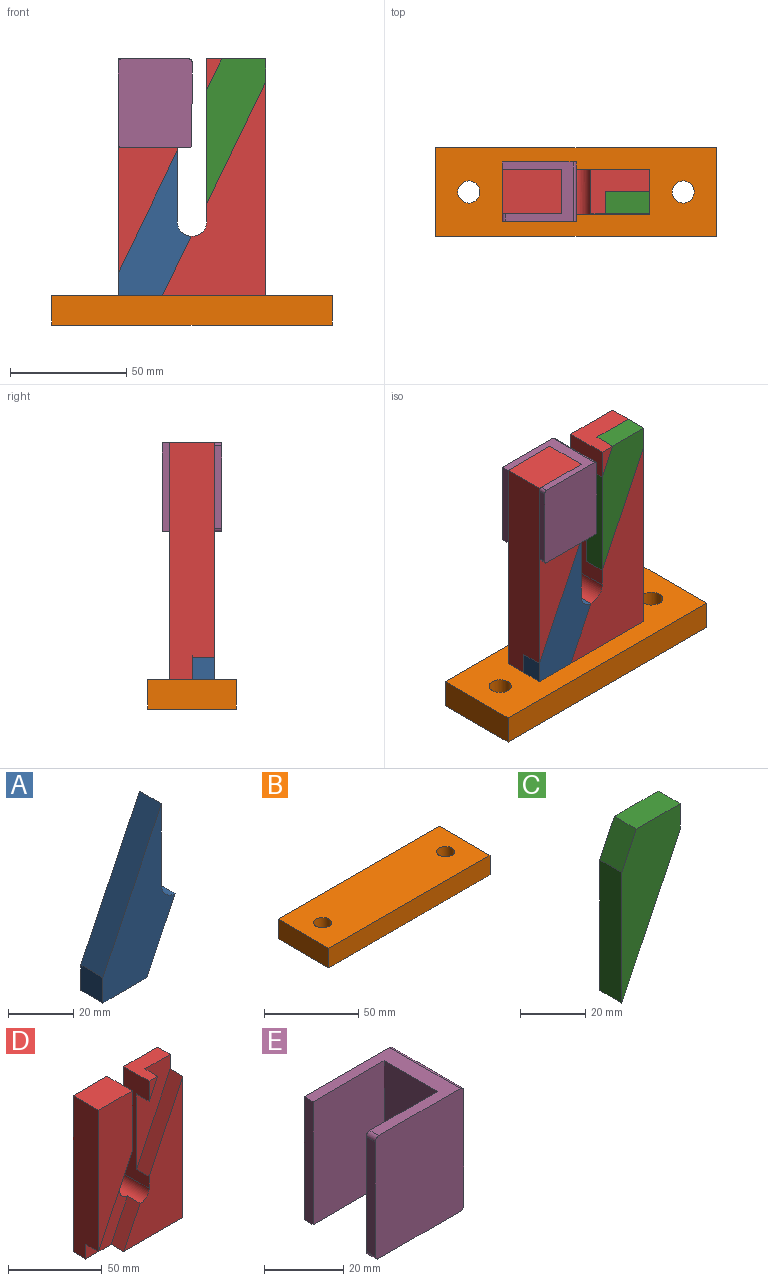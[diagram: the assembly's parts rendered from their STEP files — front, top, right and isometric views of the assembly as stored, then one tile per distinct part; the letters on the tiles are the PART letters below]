
ASSEMBLY  parts=5 mates=4
PART A: 8 faces, bbox 31.3x9.5x62.1 mm
  f0: plane 52.61x25.4mm, normal (-0.9,0,0.43), area 556.5mm2, adj f1,f5,f6,f7
  f1: plane 9.53x9.53mm, normal (-1,0,0), area 90.7mm2, adj f0,f2,f6,f7
  f2: plane 19.05x9.53mm, normal (0,0,-1), area 181.5mm2, adj f1,f3,f6,f7
  f3: plane 25.41x12.27mm, normal (0.9,0,-0.43), area 268.8mm2, adj f2,f4,f6,f7
  f4: cylinder r=6.35mm len=9.53mm, axis (0,1,0), area 90.9mm2, adj f3,f5,f6,f7
  f5: plane 30.39x9.53mm, normal (1,0,0), area 289.5mm2, adj f0,f4,f6,f7
  f6: plane 62.14x31.32mm, normal (0,-1,0), area 913.2mm2, adj f0,f1,f2,f3,f4,f5
  f7: plane 62.14x31.32mm, normal (0,1,0), area 913.2mm2, adj f0,f1,f2,f3,f4,f5
PART B: 8 faces, bbox 120.7x38.1x12.7 mm
  f0: plane 120.65x12.7mm, normal (0,-1,0), area 1532.3mm2, adj f1,f3,f4,f5
  f1: plane 38.1x12.7mm, normal (1,0,0), area 483.9mm2, adj f0,f2,f4,f5
  f2: plane 120.65x12.7mm, normal (0,1,0), area 1532.3mm2, adj f1,f3,f4,f5
  f3: plane 38.1x12.7mm, normal (-1,0,0), area 483.9mm2, adj f0,f2,f4,f5
  f4: plane 120.65x38.1mm, normal (0,0,1), area 4454.3mm2, adj f0,f1,f2,f3,f6,f7
  f5: plane 120.65x38.1mm, normal (0,0,-1), area 4454.3mm2, adj f0,f1,f2,f3,f6,f7
  f6: cylinder r=4.76mm len=12.7mm, axis (0,0,1), area 380mm2, adj f4,f5
  f7: cylinder r=4.76mm len=12.7mm, axis (0,0,1), area 380mm2, adj f4,f5
PART C: 7 faces, bbox 25.4x9.5x62.1 mm
  f0: plane 13.15x9.53mm, normal (-0.9,0,0.43), area 139.1mm2, adj f1,f4,f5,f6
  f1: plane 48.99x9.53mm, normal (-1,0,0), area 466.6mm2, adj f0,f2,f5,f6
  f2: plane 52.61x25.4mm, normal (0.9,0,-0.43), area 556.5mm2, adj f1,f3,f5,f6
  f3: plane 9.53x9.53mm, normal (1,0,0), area 90.7mm2, adj f2,f4,f5,f6
  f4: plane 19.05x9.53mm, normal (0,0,1), area 181.5mm2, adj f0,f3,f5,f6
  f5: plane 62.14x25.4mm, normal (0,-1,0), area 868.4mm2, adj f0,f1,f2,f3,f4
  f6: plane 62.14x25.4mm, normal (0,1,0), area 868.4mm2, adj f0,f1,f2,f3,f4
PART D: 18 faces, bbox 63.5x19.1x101.6 mm
  f0: plane 92.08x25.4mm, normal (0,-1,0), area 1670.5mm2, adj f6,f8,f9,f12
  f1: plane 92.08x44.45mm, normal (0,-1,0), area 2007.3mm2, adj f3,f5,f7,f11,f13,f16
  f2: plane 13.15x6.35mm, normal (0,-1,0), area 41.8mm2, adj f4,f5,f15
  f3: plane 63.5x19.05mm, normal (0,0,-1), area 1028.2mm2, adj f1,f6,f7,f10,f13,f14
  f4: plane 25.4x19.05mm, normal (0,0,1), area 302.4mm2, adj f2,f5,f7,f10,f15,f17
  f5: plane 69.85x19.05mm, normal (-1,0,0), area 864.1mm2, adj f1,f2,f4,f10,f11,f15,f16,f17
  f6: plane 101.6x19.05mm, normal (-1,0,0), area 1844.8mm2, adj f0,f3,f9,f10,f12,f14
  f7: plane 101.6x19.05mm, normal (1,0,0), area 1844.8mm2, adj f1,f3,f4,f10,f16,f17
  f8: plane 69.85x19.05mm, normal (1,0,0), area 1041.2mm2, adj f0,f9,f10,f11,f12,f14
  f9: plane 25.4x19.05mm, normal (0,0,1), area 483.9mm2, adj f0,f6,f8,f10
  f10: plane 101.6x63.5mm, normal (0,1,0), area 5501.2mm2, adj f3,f4,f5,f6,f7,f8,f9,f11
  f11: cylinder r=6.35mm len=19.05mm, axis (0,-1,0), area 289.1mm2, adj f1,f5,f8,f10,f13,f14
  f12: plane 52.61x25.4mm, normal (0.9,0,-0.43), area 556.5mm2, adj f0,f6,f8,f14
  f13: plane 25.41x12.27mm, normal (-0.9,0,0.43), area 268.8mm2, adj f1,f3,f11,f14
  f14: plane 62.14x31.32mm, normal (0,-1,0), area 913.2mm2, adj f3,f6,f8,f11,f12,f13
  f15: plane 13.15x9.53mm, normal (0.9,0,-0.43), area 139.1mm2, adj f2,f4,f5,f17
  f16: plane 52.61x25.4mm, normal (-0.9,0,0.43), area 556.5mm2, adj f1,f5,f7,f17
  f17: plane 62.14x25.4mm, normal (0,-1,0), area 868.4mm2, adj f4,f5,f7,f15,f16
PART E: 14 faces, bbox 31.8x25.4x38.1 mm
  f0: plane 38.1x19.05mm, normal (-1,0,0), area 725.8mm2, adj f1,f2,f4,f12
  f1: plane 38.1x25.4mm, normal (0,1,0), area 967mm2, adj f0,f2,f4,f5,f10,f11
  f2: plane 30.48x25.4mm, normal (0,0,-1), area 286.3mm2, adj f0,f1,f6,f7,f8,f11,f12,f13
  f3: plane 35.56x25.4mm, normal (1,0,0), area 903.2mm2, adj f6,f7,f8,f9
  f4: plane 30.48x25.4mm, normal (0,0,1), area 286.3mm2, adj f0,f1,f6,f7,f9,f10,f12,f13
  f5: plane 35.56x3.18mm, normal (-1,0,0), area 112.9mm2, adj f1,f6,f10,f11
  f6: plane 38.1x31.75mm, normal (0,-1,0), area 1208.3mm2, adj f2,f3,f4,f5,f8,f9,f10,f11
  f7: plane 38.1x31.75mm, normal (0,1,0), area 1209mm2, adj f2,f3,f4,f8,f9,f13
  f8: cylinder r=1.27mm len=25.4mm, axis (0,-1,0), area 50.7mm2, adj f2,f3,f6,f7
  f9: cylinder r=1.27mm len=25.4mm, axis (0,1,0), area 50.7mm2, adj f3,f4,f6,f7
  f10: cylinder r=1.27mm len=3.18mm, axis (0,-1,0), area 6.3mm2, adj f1,f4,f5,f6
  f11: cylinder r=1.27mm len=3.18mm, axis (0,1,0), area 6.3mm2, adj f1,f2,f5,f6
  f12: plane 38.1x25.4mm, normal (0,-1,0), area 967.7mm2, adj f0,f2,f4,f13
  f13: plane 38.1x3.18mm, normal (-1,0,0), area 121mm2, adj f2,f4,f7,f12
PLACE A t=(-55.48,-55.94,-19.05)mm
PLACE B t=(-55.48,-74.99,-82.55)mm
PLACE C t=(-55.48,-55.94,-19.05)mm
PLACE D t=(-55.48,-65.46,-19.05)mm
PLACE E t=(-71.35,-84.51,12.7)mm
MATE fastened C.f6 <-> D.f14  axis (0,1,0) through (-87.23,-74.99,-69.85)mm
MATE fastened A.f7 <-> D.f14  axis (0,1,0) through (-87.23,-74.99,-69.85)mm
MATE fastened E.f0 <-> D.f8  axis (-1,0,0) through (-61.83,-74.99,31.75)mm
MATE fastened D.f3 <-> B.f4  axis (0,0,-1) through (-55.48,-65.46,-69.85)mm
